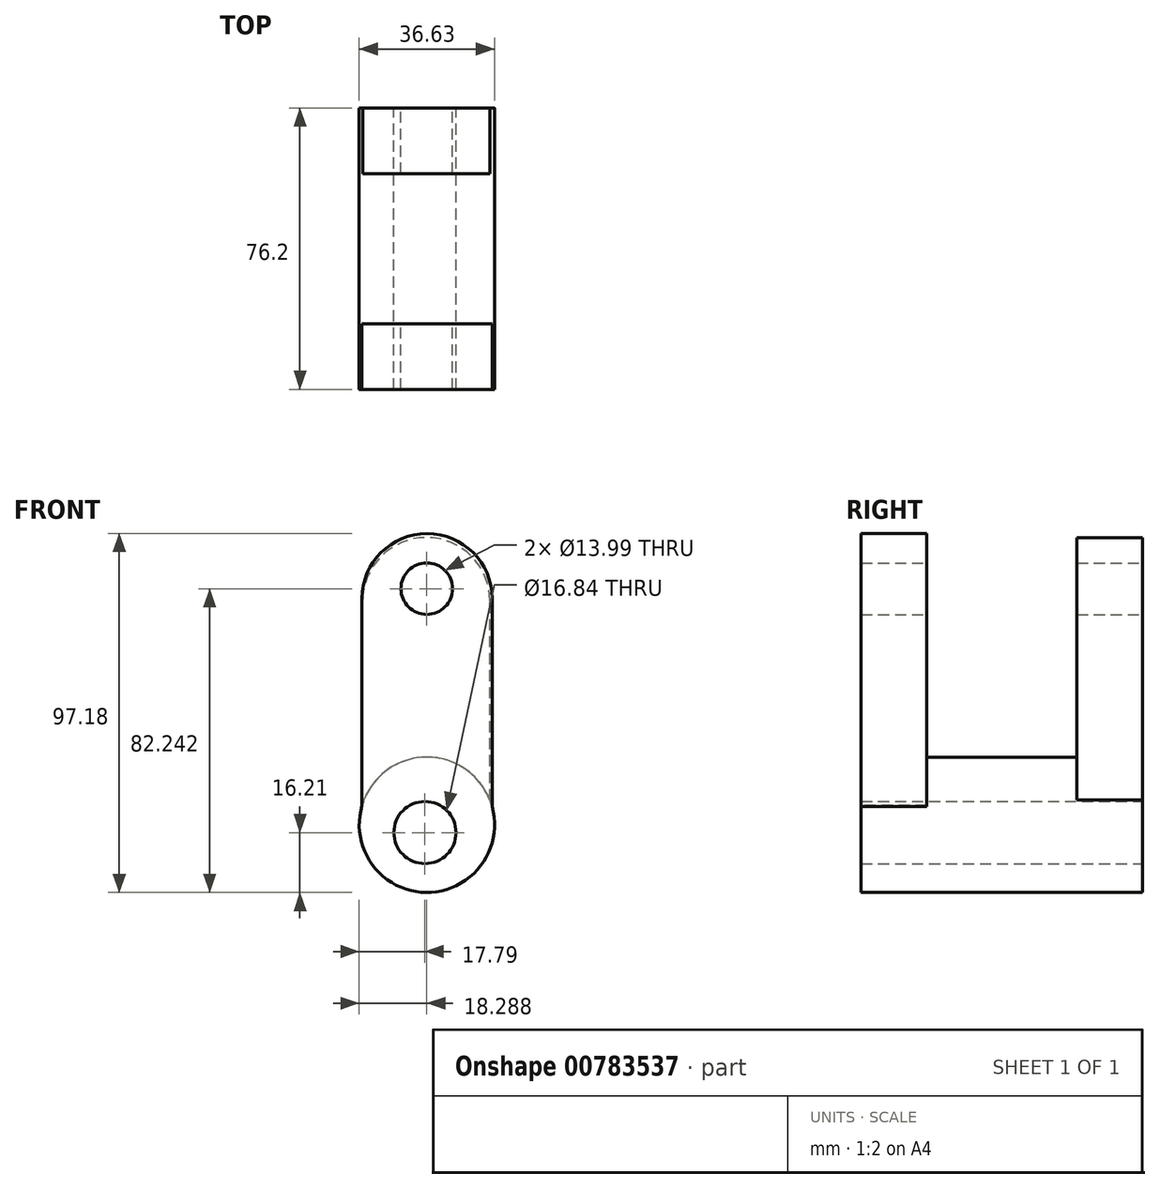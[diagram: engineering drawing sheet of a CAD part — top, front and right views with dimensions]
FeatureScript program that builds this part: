
annotation { "Feature Type Name" : "Feature", "Feature Type Description" : "" }
export const myFeature = defineFeature(function(context is Context, id is Id, definition is map)
    precondition{}
    {
        {
            var Q0;
            Q0=qCreatedBy(makeId("Front.planeOp"),FACE);
            var sketch = newSketch(context, id + "F0", { "sketchPlane" : qUnion([Q0])});
            skCircle(sketch, "E0", {"center": v(-23.06, -12.48) * mm, "radius": 18.32 * mm});
            skSolve(sketch);
        }
        {
            var Q0;
            Q0=makeQuery(id+"F0.imprint","IMPRINT",FACE,{"disambiguationData":[TD([[makeQuery(id+"F0.imprint","IMPRINT",EDGE,{"derivedFrom":sQuery(id+"F0.wireOp",EDGE,"E0")}),1.0]])]});
            extrude(context, id + "F1", {"entities" : qUnion([Q0]), "oppositeDirection" : true, "depth" : 76.2 * mm, "offsetDistance" : 25.4 * mm});
        }
        {
            var Q0;
            Q0=qCreatedBy(makeId("Front.planeOp"),FACE);
            var sketch = newSketch(context, id + "F2", { "sketchPlane" : qUnion([Q0])});
            skLineSegment(sketch, "E1.bottom", {"start": v(-40.6, -7.6) * mm, "end": v(-5.42, -7.6) * mm});
            skLineSegment(sketch, "E1.top", {"start": v(-40.6, 48.8) * mm, "end": v(-5.42, 48.8) * mm});
            skLineSegment(sketch, "E1.left", {"start": v(-40.6, -7.6) * mm, "end": v(-40.6, 48.8) * mm});
            skLineSegment(sketch, "E1.right", {"start": v(-5.42, -7.6) * mm, "end": v(-5.42, 48.8) * mm});
            skSolve(sketch);
        }
        {
            var Q0;
            Q0=makeQuery(id+"F2.imprint","IMPRINT",FACE,{"disambiguationData":[TD([[makeQuery(id+"F2.imprint","IMPRINT",EDGE,{"derivedFrom":sQuery(id+"F2.wireOp",EDGE,"E1.bottom")}),1.0]])]});
            extrude(context, id + "F3", {"entities" : qUnion([Q0]), "operationType" : NewBodyOperationType.ADD, "oppositeDirection" : true, "depth" : 17.78 * mm, "offsetDistance" : 25.4 * mm});
        }
        {
            var Q0;
            Q0=makeQuery(id+"F1.opExtrude","CAP_FACE",FACE,{"disambiguationData":[OSD([sQuery(id+"F0.wireOp",EDGE,"E0")])],"isStart":false});
            var sketch = newSketch(context, id + "F4", { "sketchPlane" : qUnion([Q0])});
            skLineSegment(sketch, "E2.bottom", {"start": v(6, -5.81) * mm, "end": v(40.44, -5.81) * mm});
            skLineSegment(sketch, "E2.top", {"start": v(6, 48.08) * mm, "end": v(40.44, 48.08) * mm});
            skLineSegment(sketch, "E2.left", {"start": v(6, -5.81) * mm, "end": v(6, 48.08) * mm});
            skLineSegment(sketch, "E2.right", {"start": v(40.44, -5.81) * mm, "end": v(40.44, 48.08) * mm});
            skSolve(sketch);
        }
        {
            var Q0;
            Q0=makeQuery(id+"F4.imprint","IMPRINT",FACE,{"disambiguationData":[TD([[makeQuery(id+"F4.imprint","IMPRINT",EDGE,{"derivedFrom":sQuery(id+"F4.wireOp",EDGE,"E2.top")}),-1.0]])]});
            extrude(context, id + "F5", {"entities" : qUnion([Q0]), "operationType" : NewBodyOperationType.ADD, "oppositeDirection" : true, "depth" : 17.78 * mm, "offsetDistance" : 25.4 * mm});
        }
        {
            var Q0;
            Q0=makeQuery(id+"F3.boolean.opBoolean","MERGE",FACE,{"derivedFrom":[makeQuery(id+"F1.opExtrude","CAP_FACE",FACE,{"disambiguationData":[OSD([sQuery(id+"F0.wireOp",EDGE,"E0")])],"isStart":true}),makeQuery(id+"F3.opExtrude","CAP_FACE",FACE,{"disambiguationData":[OSD([sQuery(id+"F2.wireOp",EDGE,"E1.bottom"),sQuery(id+"F2.wireOp",EDGE,"E1.top"),sQuery(id+"F2.wireOp",EDGE,"E1.left"),sQuery(id+"F2.wireOp",EDGE,"E1.right")])],"isStart":true})]});
            var sketch = newSketch(context, id + "F6", { "sketchPlane" : qUnion([Q0])});
            skCircle(sketch, "E3", {"center": v(-23.01, 48.8) * mm, "radius": 17.6 * mm});
            skSolve(sketch);
        }
        {
            var Q0;
            {var subQ1=makeQuery(id+"F3.opExtrude","CAP_EDGE",EDGE,{"disambiguationData":[OSD([sQuery(id+"F2.wireOp",EDGE,"E1.top")])],"isStart":true});Q0=makeQuery(id+"F6.imprint","IMPRINT",FACE,{"disambiguationData":[TD([[makeQuery(id+"F6.imprint","IMPRINT",EDGE,{"derivedFrom":subQ1}),1.0]])]});}
            extrude(context, id + "F7", {"entities" : qUnion([Q0]), "operationType" : NewBodyOperationType.ADD, "oppositeDirection" : true, "depth" : 17.78 * mm, "offsetDistance" : 25.4 * mm});
        }
        {
            var Q0;
            {var subQ0=sQuery(id+"F0.wireOp",EDGE,"E0");Q0=makeQuery(id+"F5.boolean.opBoolean","MERGE",FACE,{"derivedFrom":[makeQuery(id+"F1.opExtrude","CAP_FACE",FACE,{"disambiguationData":[OSD([subQ0])],"isStart":false}),makeQuery(id+"F5.opExtrude","CAP_FACE",FACE,{"disambiguationData":[OSD([subQ0,sQuery(id+"F4.wireOp",EDGE,"E2.bottom"),sQuery(id+"F4.wireOp",EDGE,"E2.top"),sQuery(id+"F4.wireOp",EDGE,"E2.left"),sQuery(id+"F4.wireOp",EDGE,"E2.right")])],"isStart":true})]});}
            var sketch = newSketch(context, id + "F8", { "sketchPlane" : qUnion([Q0])});
            skCircle(sketch, "E4", {"center": v(23.22, 48.08) * mm, "radius": 17.22 * mm});
            skSolve(sketch);
        }
        {
            var Q0;
            {var subQ1=makeQuery(id+"F5.opExtrude","CAP_EDGE",EDGE,{"disambiguationData":[OSD([sQuery(id+"F4.wireOp",EDGE,"E2.top")])],"isStart":true});Q0=makeQuery(id+"F8.imprint","IMPRINT",FACE,{"disambiguationData":[TD([[makeQuery(id+"F8.imprint","IMPRINT",EDGE,{"derivedFrom":subQ1}),1.0]])]});}
            extrude(context, id + "F9", {"entities" : qUnion([Q0]), "operationType" : NewBodyOperationType.ADD, "oppositeDirection" : true, "depth" : 17.78 * mm, "offsetDistance" : 25.4 * mm});
        }
        {
            var Q0;
            {var subQ0=sQuery(id+"F4.wireOp",EDGE,"E2.top");var subQ1=sQuery(id+"F0.wireOp",EDGE,"E0");Q0=makeQuery(id+"F9.boolean.opBoolean","MERGE",FACE,{"derivedFrom":[makeQuery(id+"F5.boolean.opBoolean","MERGE",FACE,{"derivedFrom":[makeQuery(id+"F1.opExtrude","CAP_FACE",FACE,{"disambiguationData":[OSD([subQ1])],"isStart":false}),makeQuery(id+"F5.opExtrude","CAP_FACE",FACE,{"disambiguationData":[OSD([subQ1,sQuery(id+"F4.wireOp",EDGE,"E2.bottom"),subQ0,sQuery(id+"F4.wireOp",EDGE,"E2.left"),sQuery(id+"F4.wireOp",EDGE,"E2.right")])],"isStart":true})]}),makeQuery(id+"F9.opExtrude","CAP_FACE",FACE,{"disambiguationData":[OSD([subQ0,sQuery(id+"F8.wireOp",EDGE,"E4")])],"isStart":true})]});}
            var sketch = newSketch(context, id + "F10", { "sketchPlane" : qUnion([Q0])});
            skCircle(sketch, "E5", {"center": v(23.1, 51.45) * mm, "radius": 7 * mm});
            skSolve(sketch);
        }
        {
            var Q0;
            Q0=makeQuery(id+"F10.imprint","IMPRINT",FACE,{"disambiguationData":[TD([[makeQuery(id+"F10.imprint","IMPRINT",EDGE,{"derivedFrom":sQuery(id+"F10.wireOp",EDGE,"E5")}),1.0]])]});
            extrude(context, id + "F11", {"entities" : qUnion([Q0]), "operationType" : NewBodyOperationType.REMOVE, "oppositeDirection" : true, "depth" : 127 * mm, "offsetDistance" : 25.4 * mm});
        }
        {
            var Q0;
            {var subQ0=sQuery(id+"F4.wireOp",EDGE,"E2.top");var subQ1=sQuery(id+"F0.wireOp",EDGE,"E0");Q0=makeQuery(id+"F9.boolean.opBoolean","MERGE",FACE,{"derivedFrom":[makeQuery(id+"F5.boolean.opBoolean","MERGE",FACE,{"derivedFrom":[makeQuery(id+"F1.opExtrude","CAP_FACE",FACE,{"disambiguationData":[OSD([subQ1])],"isStart":false}),makeQuery(id+"F5.opExtrude","CAP_FACE",FACE,{"disambiguationData":[OSD([subQ1,sQuery(id+"F4.wireOp",EDGE,"E2.bottom"),subQ0,sQuery(id+"F4.wireOp",EDGE,"E2.left"),sQuery(id+"F4.wireOp",EDGE,"E2.right")])],"isStart":true})]}),makeQuery(id+"F9.opExtrude","CAP_FACE",FACE,{"disambiguationData":[OSD([subQ0,sQuery(id+"F8.wireOp",EDGE,"E4")])],"isStart":true})]});}
            var sketch = newSketch(context, id + "F12", { "sketchPlane" : qUnion([Q0])});
            skCircle(sketch, "E6", {"center": v(23.6, -14.58) * mm, "radius": 8.42 * mm});
            skSolve(sketch);
        }
        {
            var Q0;
            Q0=makeQuery(id+"F12.imprint","IMPRINT",FACE,{"disambiguationData":[TD([[makeQuery(id+"F12.imprint","IMPRINT",EDGE,{"derivedFrom":sQuery(id+"F12.wireOp",EDGE,"E6")}),1.0]])]});
            extrude(context, id + "F13", {"entities" : qUnion([Q0]), "operationType" : NewBodyOperationType.REMOVE, "oppositeDirection" : true, "depth" : 127 * mm, "offsetDistance" : 25.4 * mm});
        }
    });
